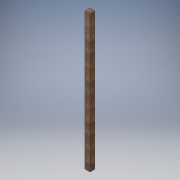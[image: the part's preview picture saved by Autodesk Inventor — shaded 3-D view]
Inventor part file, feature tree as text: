
AUTODESK INVENTOR PART (.ipt)
format: ipt  version: 2017 (Build 210142000, 142)  size: 96,768 bytes
history: native  units: in
note: dims shown in document units (in); Inventor stores cm internally (conversion verified against a paired STEP export)
features: extrude x1, sketch x1
ambient origin geometry x8: Origin, YZ Plane, XZ Plane, XY Plane, X Axis, Y Axis, Z Axis, Center Point
bodies: Solid1 (feature_tree)
feature tree (2):
  extrude  "Extrusion1"  Depth=3.5in
  sketch  "Sketch1"  dims[d0=3.5in d1=3.5in d2=96.0in d3=0.0in]
